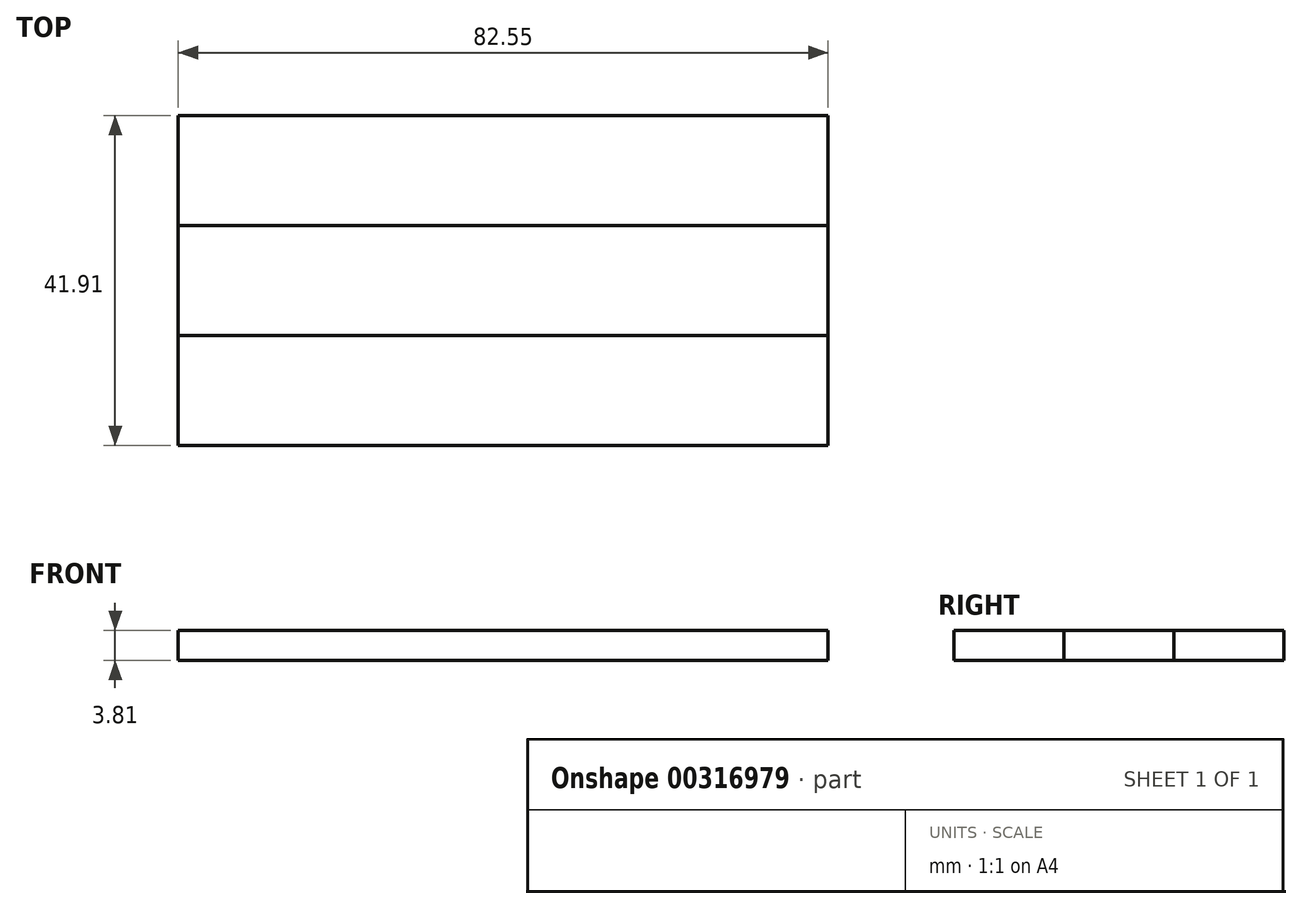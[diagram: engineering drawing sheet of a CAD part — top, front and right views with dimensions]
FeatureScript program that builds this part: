
annotation { "Feature Type Name" : "Feature", "Feature Type Description" : "" }
export const myFeature = defineFeature(function(context is Context, id is Id, definition is map)
    precondition{}
    {
        {
            var Q0;
            Q0=qCreatedBy(makeId("Top.planeOp"),FACE);
            var sketch = newSketch(context, id + "F0", { "sketchPlane" : qUnion([Q0])});
            skLineSegment(sketch, "E0.bottom", {"start": v(-37.8, 62.6) * mm, "end": v(44.74, 62.6) * mm});
            skLineSegment(sketch, "E0.top", {"start": v(-37.8, 48.63) * mm, "end": v(44.74, 48.63) * mm});
            skLineSegment(sketch, "E0.left", {"start": v(-37.8, 62.6) * mm, "end": v(-37.8, 48.63) * mm});
            skLineSegment(sketch, "E0.right", {"start": v(44.74, 62.6) * mm, "end": v(44.74, 48.63) * mm});
            skSolve(sketch);
        }
        {
            var Q0;
            Q0=makeQuery(id+"F0.imprint","IMPRINT",FACE,{"disambiguationData":[TD([[makeQuery(id+"F0.imprint","IMPRINT",EDGE,{"derivedFrom":sQuery(id+"F0.wireOp",EDGE,"E0.bottom")}),-1.0]])]});
            extrude(context, id + "F1", {"entities" : qUnion([Q0]), "depth" : 3.8 * mm});
        }
        {
            var Q0;
            Q0=makeQuery(id+"F1.opExtrude","SWEPT_BODY",BODY,{"disambiguationData":[OSD([sQuery(id+"F0.wireOp",EDGE,"E0.bottom"),sQuery(id+"F0.wireOp",EDGE,"E0.top"),sQuery(id+"F0.wireOp",EDGE,"E0.left"),sQuery(id+"F0.wireOp",EDGE,"E0.right")])]});
            transform(context, id + "F2", {"entities" : qUnion([Q0]), "transformType" : TransformType.TRANSLATION_3D, "dx" : 0 * mm, "dy" : -13.97 * mm, "dz" : 0 * mm, "makeCopy" : true});
        }
        {
            var Q0;
            Q0=makeQuery(id+"F2.opPattern","COPY",BODY,{"derivedFrom":makeQuery(id+"F1.opExtrude","SWEPT_BODY",BODY,{"disambiguationData":[OSD([sQuery(id+"F0.wireOp",EDGE,"E0.bottom"),sQuery(id+"F0.wireOp",EDGE,"E0.top"),sQuery(id+"F0.wireOp",EDGE,"E0.left"),sQuery(id+"F0.wireOp",EDGE,"E0.right")])]}),"instanceName":"1"});
            transform(context, id + "F3", {"entities" : qUnion([Q0]), "transformType" : TransformType.TRANSLATION_3D, "dx" : 0 * mm, "dy" : -13.97 * mm, "dz" : 0 * mm, "makeCopy" : true});
        }
    });
